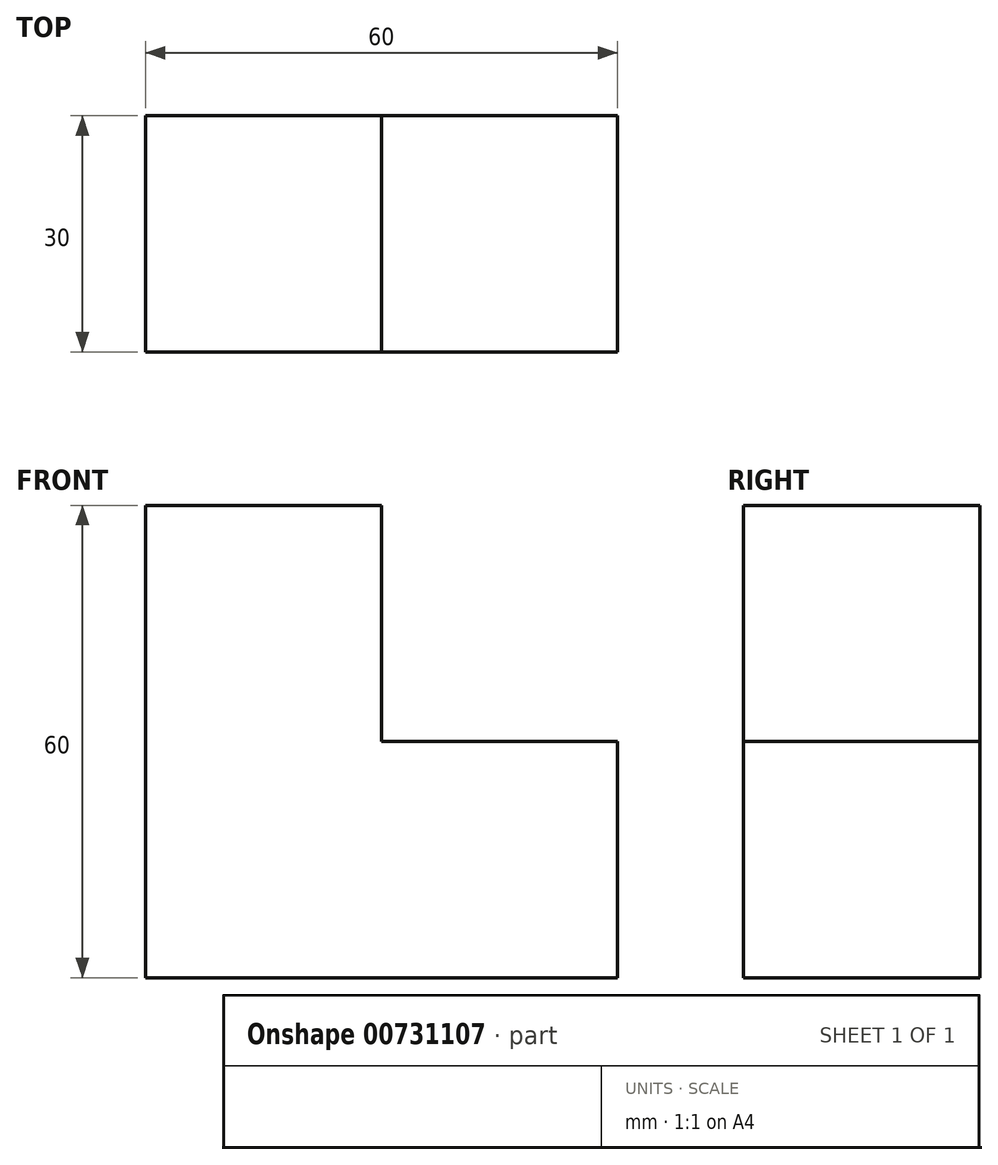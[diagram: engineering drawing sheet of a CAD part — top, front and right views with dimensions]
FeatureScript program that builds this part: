
annotation { "Feature Type Name" : "Feature", "Feature Type Description" : "" }
export const myFeature = defineFeature(function(context is Context, id is Id, definition is map)
    precondition{}
    {
        {
            var Q0;
            Q0=qCreatedBy(makeId("Front.planeOp"),FACE);
            var sketch = newSketch(context, id + "F0", { "sketchPlane" : qUnion([Q0])});
            skLineSegment(sketch, "E0.bottom", {"start": v(-30, 30) * mm, "end": v(0, 30) * mm});
            skLineSegment(sketch, "E0.top", {"start": v(-30, -30) * mm, "end": v(30, -30) * mm});
            skLineSegment(sketch, "E0.left", {"start": v(-30, 30) * mm, "end": v(-30, -30) * mm});
            skLineSegment(sketch, "E0.right", {"start": v(30, 0) * mm, "end": v(30, -30) * mm});
            skPoint(sketch, "E0.middle", {"position": v(0, 0) * mm});
            skLineSegment(sketch, "E1", {"start": v(0, 30) * mm, "end": v(0, 0) * mm});
            skLineSegment(sketch, "E2", {"start": v(30, 0) * mm, "end": v(0, 0) * mm});
            skPoint(sketch, "E3.orphan", {"position": v(30, 30) * mm});
            skSolve(sketch);
        }
        {
            var Q0;
            Q0 = qSketchRegion(id + "F0", true);
            extrude(context, id + "F1", {"entities" : qUnion([Q0]), "depth" : 30 * mm, "offsetDistance" : 25 * mm});
        }
    });
